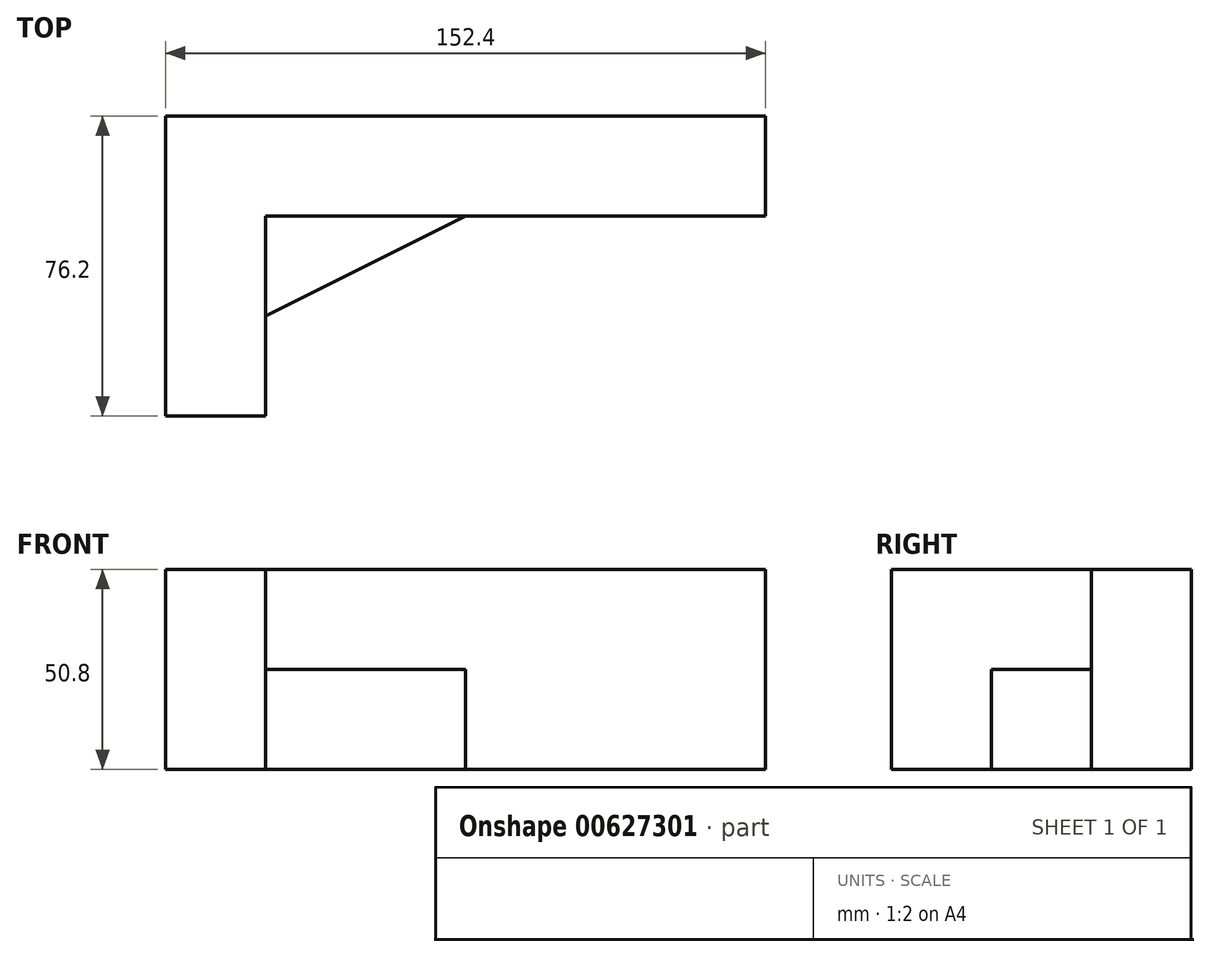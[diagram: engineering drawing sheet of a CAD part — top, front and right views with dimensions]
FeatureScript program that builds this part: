
annotation { "Feature Type Name" : "Feature", "Feature Type Description" : "" }
export const myFeature = defineFeature(function(context is Context, id is Id, definition is map)
    precondition{}
    {
        {
            var Q0;
            Q0=qCreatedBy(makeId("Front.planeOp"),FACE);
            var sketch = newSketch(context, id + "F0", { "sketchPlane" : qUnion([Q0])});
            skLineSegment(sketch, "E0.bottom", {"start": v(0, 0) * mm, "end": v(152.4, 0) * mm});
            skLineSegment(sketch, "E0.top", {"start": v(0, 50.8) * mm, "end": v(152.4, 50.8) * mm});
            skLineSegment(sketch, "E0.left", {"start": v(0, 0) * mm, "end": v(0, 50.8) * mm});
            skLineSegment(sketch, "E0.right", {"start": v(152.4, 0) * mm, "end": v(152.4, 50.8) * mm});
            skLineSegment(sketch, "E1", {"start": v(0, 50.8) * mm, "end": v(25.4, 50.8) * mm});
            skLineSegment(sketch, "E2", {"start": v(25.4, 50.8) * mm, "end": v(25.4, 0) * mm});
            skLineSegment(sketch, "E3.bottom", {"start": v(76.2, 0) * mm, "end": v(25.4, 0) * mm});
            skLineSegment(sketch, "E3.top", {"start": v(76.2, 50.8) * mm, "end": v(25.4, 50.8) * mm});
            skLineSegment(sketch, "E3.left", {"start": v(76.2, 0) * mm, "end": v(76.2, 50.8) * mm});
            skLineSegment(sketch, "E3.right", {"start": v(25.4, 0) * mm, "end": v(25.4, 50.8) * mm});
            skLineSegment(sketch, "E4", {"start": v(0, 0) * mm, "end": v(25.4, 0) * mm});
            skLineSegment(sketch, "E5", {"start": v(25.4, 25.4) * mm, "end": v(76.2, 25.4) * mm});
            skSolve(sketch);
        }
        {
            var Q0;
            Q0 = qSketchRegion(id + "F0", true);
            extrude(context, id + "F1", {"entities" : qUnion([Q0]), "depth" : 25.4 * mm, "offsetDistance" : 25.4 * mm});
        }
        {
            var Q0;
            Q0=makeQuery(id+"F1.opExtrude","CAP_FACE",FACE,{"disambiguationData":[OSD([sQuery(id+"F0.wireOp",EDGE,"E0.bottom"),sQuery(id+"F0.wireOp",EDGE,"E0.top"),sQuery(id+"F0.wireOp",EDGE,"E0.left"),sQuery(id+"F0.wireOp",EDGE,"E0.right"),sQuery(id+"F0.wireOp",EDGE,"E1"),sQuery(id+"F0.wireOp",EDGE,"E3.bottom"),sQuery(id+"F0.wireOp",EDGE,"E3.top"),sQuery(id+"F0.wireOp",EDGE,"E4")])],"isStart":false});
            var sketch = newSketch(context, id + "F2", { "sketchPlane" : qUnion([Q0])});
            skLineSegment(sketch, "E6", {"start": v(0, 0) * mm, "end": v(25.4, 0) * mm});
            skLineSegment(sketch, "E7", {"start": v(25.4, 25.4) * mm, "end": v(76.2, 25.4) * mm});
            skLineSegment(sketch, "E8", {"start": v(25.4, 0) * mm, "end": v(76.2, 0) * mm});
            skLineSegment(sketch, "E9", {"start": v(76.2, 25.4) * mm, "end": v(76.2, 0) * mm});
            skLineSegment(sketch, "E10", {"start": v(25.4, 0) * mm, "end": v(25.4, 50.8) * mm});
            skSolve(sketch);
        }
        {
            var Q0;
            {var subQ2=sQuery(id+"F2.wireOp",EDGE,"E6");Q0=makeQuery(id+"F2.imprint","IMPRINT",FACE,{"disambiguationData":[TD([[makeQuery(id+"F2.imprint","IMPRINT",EDGE,{"derivedFrom":subQ2}),1.0]])]});}
            var Q1;
            {var subQ0=sQuery(id+"F2.wireOp",EDGE,"E7");Q1=makeQuery(id+"F2.imprint","IMPRINT",FACE,{"disambiguationData":[TD([[makeQuery(id+"F2.imprint","IMPRINT",EDGE,{"derivedFrom":subQ0}),-1.0]])]});}
            var Q2;
            {var subQ1=sQuery(id+"F2.wireOp",EDGE,"E7");Q2=makeQuery(id+"F2.imprint","IMPRINT",FACE,{"disambiguationData":[TD([[makeQuery(id+"F2.imprint","IMPRINT",EDGE,{"derivedFrom":subQ1}),1.0]])]});}
            extrude(context, id + "F3", {"entities" : qUnion([Q0, Q1, Q2]), "operationType" : NewBodyOperationType.ADD, "oppositeDirection" : true, "depth" : 76.2 * mm, "offsetDistance" : 25.4 * mm});
        }
        {
            var Q0;
            Q0=makeQuery(id+"F1.opExtrude","CAP_FACE",FACE,{"disambiguationData":[OSD([sQuery(id+"F0.wireOp",EDGE,"E0.bottom"),sQuery(id+"F0.wireOp",EDGE,"E0.top"),sQuery(id+"F0.wireOp",EDGE,"E0.left"),sQuery(id+"F0.wireOp",EDGE,"E0.right"),sQuery(id+"F0.wireOp",EDGE,"E1"),sQuery(id+"F0.wireOp",EDGE,"E3.bottom"),sQuery(id+"F0.wireOp",EDGE,"E3.top"),sQuery(id+"F0.wireOp",EDGE,"E4")])],"isStart":false});
            var sketch = newSketch(context, id + "F4", { "sketchPlane" : qUnion([Q0])});
            skLineSegment(sketch, "E11", {"start": v(25.4, 0) * mm, "end": v(25.4, 50.8) * mm});
            skLineSegment(sketch, "E12", {"start": v(76.2, 0) * mm, "end": v(76.2, 50.8) * mm});
            skLineSegment(sketch, "E13", {"start": v(0, 0) * mm, "end": v(25.4, 0) * mm});
            skLineSegment(sketch, "E14", {"start": v(76.2, 0) * mm, "end": v(25.4, 0) * mm});
            skLineSegment(sketch, "E15", {"start": v(76.2, 0) * mm, "end": v(152.4, 0) * mm});
            skLineSegment(sketch, "E16", {"start": v(25.4, 25.4) * mm, "end": v(76.2, 25.4) * mm});
            skSolve(sketch);
        }
        {
            var Q0;
            {var subQ3=sQuery(id+"F4.wireOp",EDGE,"E16");Q0=makeQuery(id+"F4.imprint","IMPRINT",FACE,{"disambiguationData":[TD([[makeQuery(id+"F4.imprint","IMPRINT",EDGE,{"derivedFrom":subQ3}),1.0]])]});}
            extrude(context, id + "F5", {"entities" : qUnion([Q0]), "operationType" : NewBodyOperationType.REMOVE, "oppositeDirection" : true, "depth" : 50.8 * mm, "offsetDistance" : 25.4 * mm});
        }
        {
            var Q0;
            Q0=makeQuery(id+"F1.opExtrude","CAP_FACE",FACE,{"disambiguationData":[OSD([sQuery(id+"F0.wireOp",EDGE,"E0.bottom"),sQuery(id+"F0.wireOp",EDGE,"E0.top"),sQuery(id+"F0.wireOp",EDGE,"E0.left"),sQuery(id+"F0.wireOp",EDGE,"E0.right"),sQuery(id+"F0.wireOp",EDGE,"E1"),sQuery(id+"F0.wireOp",EDGE,"E3.bottom"),sQuery(id+"F0.wireOp",EDGE,"E3.top"),sQuery(id+"F0.wireOp",EDGE,"E4")])],"isStart":false});
            var sketch = newSketch(context, id + "F6", { "sketchPlane" : qUnion([Q0])});
            skLineSegment(sketch, "E17", {"start": v(25.4, 25.4) * mm, "end": v(25.4, 0) * mm});
            skLineSegment(sketch, "E18", {"start": v(76.2, 25.4) * mm, "end": v(76.2, 0) * mm});
            skSolve(sketch);
        }
        {
            var Q0;
            {var subQ0=sQuery(id+"F6.wireOp",EDGE,"E17");Q0=makeQuery(id+"F6.imprint","IMPRINT",FACE,{"disambiguationData":[TD([[makeQuery(id+"F6.imprint","IMPRINT",EDGE,{"derivedFrom":subQ0}),1.0]])]});}
            extrude(context, id + "F7", {"entities" : qUnion([Q0]), "operationType" : NewBodyOperationType.REMOVE, "oppositeDirection" : true, "depth" : 25.4 * mm, "offsetDistance" : 25.4 * mm});
        }
        {
            var Q0;
            {var subQ0=sQuery(id+"F0.wireOp",EDGE,"E0.right");var subQ1=sQuery(id+"F0.wireOp",EDGE,"E4");var subQ2=sQuery(id+"F0.wireOp",EDGE,"E3.bottom");var subQ3=sQuery(id+"F0.wireOp",EDGE,"E0.bottom");var subQ4=sQuery(id+"F0.wireOp",EDGE,"E3.top");var subQ5=sQuery(id+"F0.wireOp",EDGE,"E1");var subQ6=sQuery(id+"F0.wireOp",EDGE,"E0.top");Q0=makeQuery(id+"F7.boolean.opBoolean","SPLIT",FACE,{"disambiguationData":[TD([makeQuery(id+"F1.opExtrude","SWEPT_FACE",FACE,{"disambiguationData":[OSD([subQ0])]})])],"derivedFrom":makeQuery(id+"F1.opExtrude","CAP_FACE",FACE,{"disambiguationData":[OSD([subQ3,subQ6,sQuery(id+"F0.wireOp",EDGE,"E0.left"),subQ0,subQ5,subQ2,subQ4,subQ1])],"isStart":false})});}
            var sketch = newSketch(context, id + "F8", { "sketchPlane" : qUnion([Q0])});
            skSolve(sketch);
        }
        {
            var Q0;
            {var subQ0=sQuery(id+"F0.wireOp",EDGE,"E0.right");Q0=makeQuery(id+"F8.imprint","IMPRINT",FACE,{"disambiguationData":[TD([[makeQuery(id+"F8.imprint","IMPRINT",EDGE,{"derivedFrom":makeQuery(id+"F1.opExtrude","CAP_EDGE",EDGE,{"disambiguationData":[OSD([subQ0])],"isStart":false})}),1.0]])]});}
            extrude(context, id + "F9", {"entities" : qUnion([Q0]), "operationType" : NewBodyOperationType.REMOVE, "oppositeDirection" : true, "depth" : 50.8 * mm, "offsetDistance" : 25.4 * mm});
        }
        {
            var Q0;
            Q0=makeQuery(id+"F5.boolean.opBoolean","COPY",FACE,{"derivedFrom":makeQuery(id+"F5.opExtrude","SWEPT_FACE",FACE,{"disambiguationData":[OSD([sQuery(id+"F4.wireOp",EDGE,"E16")])]})});
            var sketch = newSketch(context, id + "F10", { "sketchPlane" : qUnion([Q0])});
            skLineSegment(sketch, "E19", {"start": v(25.4, 0) * mm, "end": v(76.2, 25.4) * mm});
            skSolve(sketch);
        }
        {
            var Q0;
            Q0=makeQuery(id+"F10.imprint","IMPRINT",FACE,{"disambiguationData":[TD([[makeQuery(id+"F10.imprint","IMPRINT",EDGE,{"derivedFrom":sQuery(id+"F10.wireOp",EDGE,"E19")}),-1.0]])]});
            extrude(context, id + "F11", {"entities" : qUnion([Q0]), "operationType" : NewBodyOperationType.REMOVE, "oppositeDirection" : true, "depth" : 25.4 * mm, "offsetDistance" : 25.4 * mm});
        }
    });
